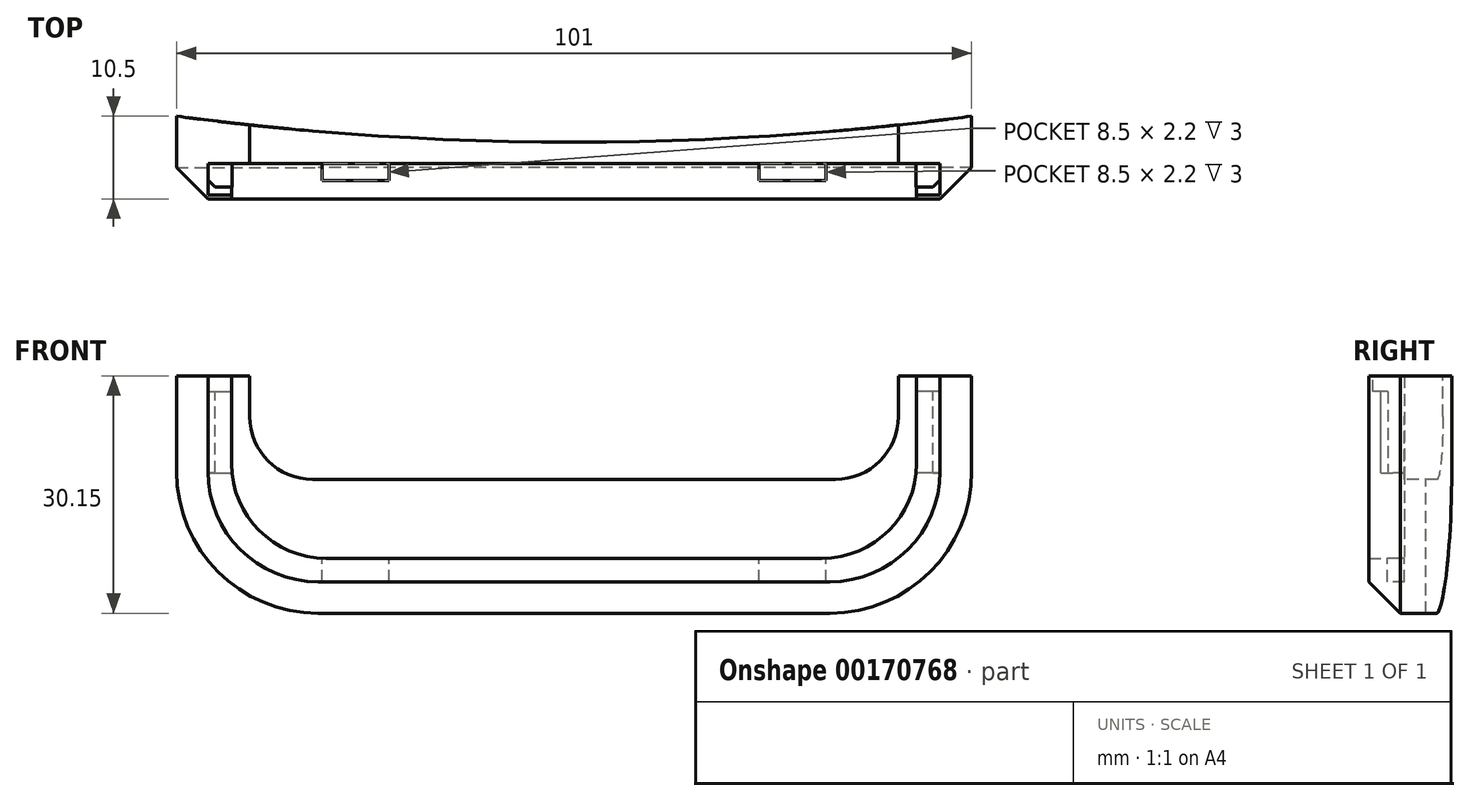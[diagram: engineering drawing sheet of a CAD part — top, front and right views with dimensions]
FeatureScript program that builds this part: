
annotation { "Feature Type Name" : "Feature", "Feature Type Description" : "" }
export const myFeature = defineFeature(function(context is Context, id is Id, definition is map)
    precondition{}
    {
        {
            var Q0;
            Q0=qCreatedBy(makeId("Front.planeOp"),FACE);
            var sketch = newSketch(context, id + "F0", { "sketchPlane" : qUnion([Q0])});
            skLineSegment(sketch, "E0", {"start": v(0, -17) * mm, "end": v(0, 17) * mm});
            skLineSegment(sketch, "E1", {"start": v(0, 17) * mm, "end": v(-31.5, 17) * mm});
            skLineSegment(sketch, "E2", {"start": v(-43.5, 5) * mm, "end": v(-43.5, -5) * mm});
            skLineSegment(sketch, "E3", {"start": v(-31.5, -17) * mm, "end": v(0, -17) * mm});
            skPoint(sketch, "E4.visualSharp", {"position": v(-43.5, 17) * mm});
            skArc(sketch, "E4.filletArc", {"start": v(-31.5, 17) * mm, "mid": v(-39.99, 13.49) * mm, "end": v(-43.5, 5) * mm});
            skPoint(sketch, "E5.visualSharp", {"position": v(-43.5, -17) * mm});
            skArc(sketch, "E5.filletArc", {"start": v(-43.5, -5) * mm, "mid": v(-39.99, -13.49) * mm, "end": v(-31.5, -17) * mm});
            skLineSegment(sketch, "E6", {"start": v(-43.5, 6.15) * mm, "end": v(-50.5, 6.15) * mm});
            skLineSegment(sketch, "E7", {"start": v(-50.5, 6.15) * mm, "end": v(-50.5, -24) * mm});
            skLineSegment(sketch, "E8", {"start": v(-50.5, -24) * mm, "end": v(0, -24) * mm});
            skLineSegment(sketch, "E9", {"start": v(0, -24) * mm, "end": v(0, -17) * mm});
            skLineSegment(sketch, "E10", {"start": v(-43.5, -6.15) * mm, "end": v(-50.5, -6.15) * mm, "construction": true});
            skLineSegment(sketch, "E11", {"start": v(-43.5, 6.15) * mm, "end": v(-43.5, 5) * mm});
            skSolve(sketch);
        }
        {
            var Q0;
            Q0=makeQuery(id+"F0.imprint","IMPRINT",FACE,{"disambiguationData":[TD([[makeQuery(id+"F0.imprint","IMPRINT",EDGE,{"derivedFrom":sQuery(id+"F0.wireOp",EDGE,"E2")}),-1.0]])]});
            extrude(context, id + "F1", {"entities" : qUnion([Q0]), "depth" : 4.5 * mm});
        }
        {
            var Q0;
            Q0=makeQuery(id+"F1.opExtrude","CAP_FACE",FACE,{"disambiguationData":[OSD([sQuery(id+"F0.wireOp",EDGE,"E2"),sQuery(id+"F0.wireOp",EDGE,"E3"),sQuery(id+"F0.wireOp",EDGE,"E5.filletArc"),sQuery(id+"F0.wireOp",EDGE,"E6"),sQuery(id+"F0.wireOp",EDGE,"E7"),sQuery(id+"F0.wireOp",EDGE,"E8"),sQuery(id+"F0.wireOp",EDGE,"E9"),sQuery(id+"F0.wireOp",EDGE,"E11")])],"isStart":true});
            var sketch = newSketch(context, id + "F2", { "sketchPlane" : qUnion([Q0])});
            skLineSegment(sketch, "E12", {"start": v(43.5, 6.15) * mm, "end": v(41.2, 6.15) * mm});
            skLineSegment(sketch, "E13", {"start": v(41.2, 6.15) * mm, "end": v(41.2, 1) * mm});
            skLineSegment(sketch, "E14", {"start": v(33.2, -7) * mm, "end": v(0, -7) * mm});
            skLineSegment(sketch, "E15", {"start": v(0, -7) * mm, "end": v(0, -24) * mm});
            skLineSegment(sketch, "E16", {"start": v(0, -24) * mm, "end": v(50.5, -24) * mm});
            skLineSegment(sketch, "E17", {"start": v(50.5, -24) * mm, "end": v(50.5, 6.15) * mm});
            skLineSegment(sketch, "E18", {"start": v(50.5, 6.15) * mm, "end": v(43.5, 6.15) * mm});
            skPoint(sketch, "E19.visualSharp", {"position": v(41.2, -7) * mm});
            skArc(sketch, "E19.filletArc", {"start": v(33.2, -7) * mm, "mid": v(38.86, -4.66) * mm, "end": v(41.2, 1) * mm});
            skSolve(sketch);
        }
        {
            var Q0;
            Q0 = qSketchRegion(id + "F2", true);
            extrude(context, id + "F3", {"entities" : qUnion([Q0]), "operationType" : NewBodyOperationType.ADD, "depth" : 6 * mm});
        }
        {
            var Q0;
            Q0=makeQuery(id+"F3.boolean.opBoolean","MERGE",EDGE,{"derivedFrom":[makeQuery(id+"F1.opExtrude","SWEPT_EDGE",EDGE,{"disambiguationData":[OSD([sQuery(id+"F0.wireOp",EDGE,"E7"),sQuery(id+"F0.wireOp",EDGE,"E8")])]}),makeQuery(id+"F3.opExtrude","SWEPT_EDGE",EDGE,{"disambiguationData":[OSD([sQuery(id+"F2.wireOp",EDGE,"E16"),sQuery(id+"F2.wireOp",EDGE,"E17")])]})]});
            fillet(context, id + "F4", {"entities" : qUnion([Q0]), "radius" : 18 * mm, "tangentPropagation" : true, "allowEdgeOverflow" : false});
        }
        {
            var Q0;
            {var subQ0=sQuery(id+"F0.wireOp",EDGE,"E8");var subQ1=sQuery(id+"F0.wireOp",EDGE,"E7");Q0=makeQuery(id+"F4.opFillet","BLEND_EDGE",EDGE,{"blendedFrom":[makeQuery(id+"F3.boolean.opBoolean","MERGE",EDGE,{"derivedFrom":[makeQuery(id+"F1.opExtrude","SWEPT_EDGE",EDGE,{"disambiguationData":[OSD([subQ1,subQ0])]}),makeQuery(id+"F3.opExtrude","SWEPT_EDGE",EDGE,{"disambiguationData":[OSD([sQuery(id+"F2.wireOp",EDGE,"E16"),sQuery(id+"F2.wireOp",EDGE,"E17")])]})]}),makeQuery(id+"F1.opExtrude","CAP_FACE",FACE,{"disambiguationData":[OSD([sQuery(id+"F0.wireOp",EDGE,"E2"),sQuery(id+"F0.wireOp",EDGE,"E3"),sQuery(id+"F0.wireOp",EDGE,"E5.filletArc"),sQuery(id+"F0.wireOp",EDGE,"E6"),subQ1,subQ0,sQuery(id+"F0.wireOp",EDGE,"E9"),sQuery(id+"F0.wireOp",EDGE,"E11")])],"isStart":false})],"blendedInto":[makeQuery(id+"F1.opExtrude","CAP_FACE",FACE,{"disambiguationData":[OSD([sQuery(id+"F0.wireOp",EDGE,"E2"),sQuery(id+"F0.wireOp",EDGE,"E3"),sQuery(id+"F0.wireOp",EDGE,"E5.filletArc"),sQuery(id+"F0.wireOp",EDGE,"E6"),subQ1,subQ0,sQuery(id+"F0.wireOp",EDGE,"E9"),sQuery(id+"F0.wireOp",EDGE,"E11")])],"isStart":false})]});}
            chamfer(context, id + "F5", {"entities" : qUnion([Q0]), "width" : 4 * mm, "tangentPropagation" : true});
        }
        {
            var Q0;
            Q0=qCreatedBy(makeId("Top.planeOp"),FACE);
            var sketch = newSketch(context, id + "F6", { "sketchPlane" : qUnion([Q0])});
            skLineSegment(sketch, "E20.bottom", {"start": v(-23.5, 0) * mm, "end": v(-32, 0) * mm});
            skLineSegment(sketch, "E20.top", {"start": v(-23.5, -2.2) * mm, "end": v(-32, -2.2) * mm});
            skLineSegment(sketch, "E20.left", {"start": v(-23.5, 0) * mm, "end": v(-23.5, -2.2) * mm});
            skLineSegment(sketch, "E20.right", {"start": v(-32, 0) * mm, "end": v(-32, -2.2) * mm});
            skSolve(sketch);
        }
        {
            var Q0;
            Q0 = qSketchRegion(id + "F6", true);
            extrude(context, id + "F7", {"entities" : qUnion([Q0]), "operationType" : NewBodyOperationType.REMOVE, "oppositeDirection" : true, "depth" : 20 * mm});
        }
        {
            var Q0;
            Q0=makeQuery(id+"F1.opExtrude","SWEPT_FACE",FACE,{"disambiguationData":[OSD([sQuery(id+"F0.wireOp",EDGE,"E2"),sQuery(id+"F0.wireOp",EDGE,"E11")])]});
            var sketch = newSketch(context, id + "F8", { "sketchPlane" : qUnion([Q0])});
            skLineSegment(sketch, "E21.bottom", {"start": v(0, -6.15) * mm, "end": v(-3, -6.15) * mm});
            skLineSegment(sketch, "E21.top", {"start": v(0, 4.15) * mm, "end": v(-3, 4.15) * mm});
            skLineSegment(sketch, "E21.left", {"start": v(0, -6.15) * mm, "end": v(0, 4.15) * mm});
            skLineSegment(sketch, "E21.right", {"start": v(-3, -6.15) * mm, "end": v(-3, 4.15) * mm});
            skLineSegment(sketch, "E22.bottom", {"start": v(0, 4.15) * mm, "end": v(-4, 4.15) * mm});
            skLineSegment(sketch, "E22.top", {"start": v(0, 6.15) * mm, "end": v(-4, 6.15) * mm});
            skLineSegment(sketch, "E22.left", {"start": v(0, 4.15) * mm, "end": v(0, 6.15) * mm});
            skLineSegment(sketch, "E22.right", {"start": v(-4, 4.15) * mm, "end": v(-4, 6.15) * mm});
            skSolve(sketch);
        }
        {
            var Q0;
            {var subQ0=sQuery(id+"F8.wireOp",EDGE,"E21.top");var subQ1=makeQuery(id+"F8.imprint","IMPRINT",EDGE,{"derivedFrom":subQ0});var subQ10=sQuery(id+"F8.wireOp",EDGE,"E21.bottom");Q0=qUnion([makeQuery(id+"F8.imprint","IMPRINT",FACE,{"disambiguationData":[TD([[subQ1,-1.0]])]}),makeQuery(id+"F8.imprint","IMPRINT",FACE,{"disambiguationData":[TD([[makeQuery(id+"F8.imprint","IMPRINT",EDGE,{"derivedFrom":subQ10}),-1.0]])]}),makeQuery(id+"F8.imprint","IMPRINT",FACE,{"disambiguationData":[TD([[subQ1,1.0]])]})]);}
            extrude(context, id + "F9", {"entities" : qUnion([Q0]), "operationType" : NewBodyOperationType.REMOVE, "oppositeDirection" : true, "depth" : 3 * mm, "hasSecondDirection" : true, "secondDirectionBound" : BoundingType.THROUGH_ALL, "secondDirectionOppositeDirection" : false, "secondDirectionDepth" : 25 * mm});
        }
        {
            var Q0;
            Q0=makeQuery(id+"F9.boolean.opBoolean","COPY",EDGE,{"derivedFrom":makeQuery(id+"F9.opExtrude","CAP_EDGE",EDGE,{"disambiguationData":[OSD([sQuery(id+"F8.wireOp",EDGE,"E21.right")])],"isStart":false})});
            chamfer(context, id + "F10", {"entities" : qUnion([Q0]), "width" : 0.9 * mm, "tangentPropagation" : true});
        }
        {
            var Q0;
            Q0=makeQuery(id+"F1.opExtrude","SWEPT_BODY",BODY,{"disambiguationData":[OSD([sQuery(id+"F0.wireOp",EDGE,"E2"),sQuery(id+"F0.wireOp",EDGE,"E3"),sQuery(id+"F0.wireOp",EDGE,"E5.filletArc"),sQuery(id+"F0.wireOp",EDGE,"E6"),sQuery(id+"F0.wireOp",EDGE,"E7"),sQuery(id+"F0.wireOp",EDGE,"E8"),sQuery(id+"F0.wireOp",EDGE,"E9"),sQuery(id+"F0.wireOp",EDGE,"E11")])]});
            var Q1;
            Q1=qCreatedBy(makeId("Right.planeOp"),FACE);
            mirror(context, id + "F11", {"operationType" : NewBodyOperationType.ADD, "entities" : qUnion([Q0]), "mirrorPlane" : qUnion([Q1])});
        }
        {
            var Q0;
            Q0=qCreatedBy(makeId("Top.planeOp"),FACE);
            var sketch = newSketch(context, id + "F12", { "sketchPlane" : qUnion([Q0])});
            skArc(sketch, "E23", {"start": v(-50.5, 6) * mm, "mid": v(0, 2.7) * mm, "end": v(50.5, 6) * mm});
            skLineSegment(sketch, "E24", {"start": v(-50.5, 6) * mm, "end": v(-50.5, 10) * mm});
            skLineSegment(sketch, "E25", {"start": v(-50.5, 10) * mm, "end": v(50.5, 10) * mm});
            skLineSegment(sketch, "E26", {"start": v(50.5, 10) * mm, "end": v(50.5, 6) * mm});
            skSolve(sketch);
        }
        {
            var Q0;
            Q0 = qSketchRegion(id + "F12", true);
            extrude(context, id + "F13", {"entities" : qUnion([Q0]), "operationType" : NewBodyOperationType.REMOVE, "endBound" : BoundingType.THROUGH_ALL, "oppositeDirection" : true, "depth" : 25 * mm, "hasSecondDirection" : true, "secondDirectionBound" : BoundingType.THROUGH_ALL, "secondDirectionOppositeDirection" : false, "secondDirectionDepth" : 25 * mm});
        }
    });
